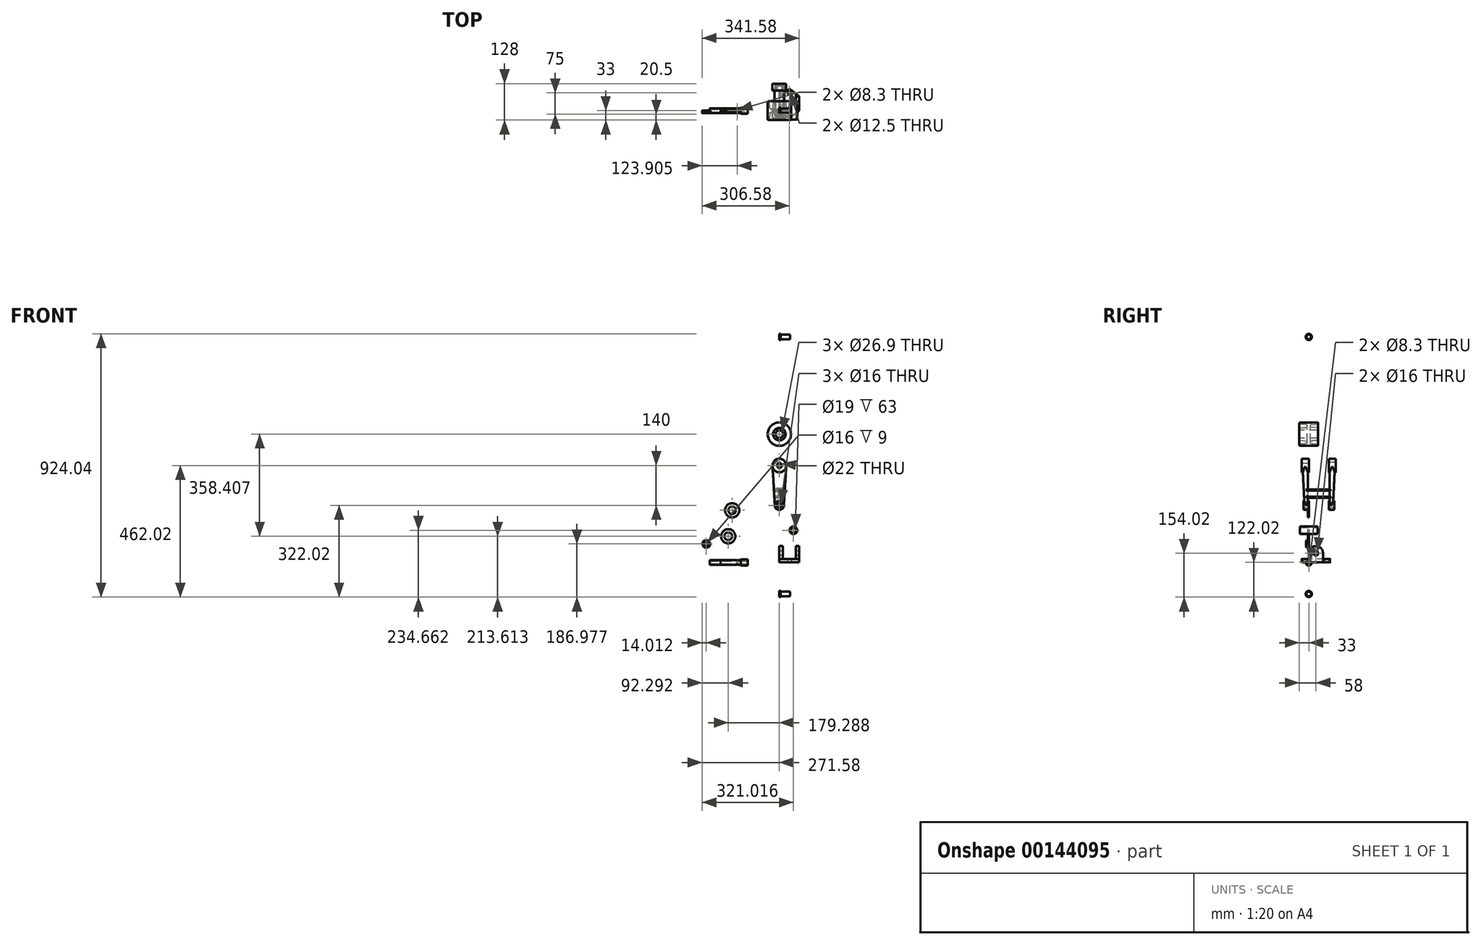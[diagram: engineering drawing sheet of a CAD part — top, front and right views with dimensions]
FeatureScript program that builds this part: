
annotation { "Feature Type Name" : "Feature", "Feature Type Description" : "" }
export const myFeature = defineFeature(function(context is Context, id is Id, definition is map)
    precondition{}
    {
        {
            var Q0;
            Q0=qCreatedBy(makeId("Top.planeOp"),FACE);
            var sketch = newSketch(context, id + "F0", { "sketchPlane" : qUnion([Q0])});
            skLineSegment(sketch, "E0", {"start": v(0, 0) * mm, "end": v(0, 50) * mm});
            skLineSegment(sketch, "E1", {"start": v(0, 50) * mm, "end": v(27.53, 71.9) * mm});
            skLineSegment(sketch, "E2", {"start": v(42.47, 71.9) * mm, "end": v(70, 50) * mm});
            skLineSegment(sketch, "E3", {"start": v(70, 50) * mm, "end": v(70, 0) * mm});
            skLineSegment(sketch, "E4", {"start": v(70, 0) * mm, "end": v(42.47, -21.9) * mm});
            skLineSegment(sketch, "E5", {"start": v(27.53, -21.9) * mm, "end": v(0, 0) * mm});
            skPoint(sketch, "E6.visualSharp", {"position": v(35, 77.83) * mm});
            skArc(sketch, "E6.filletArc", {"start": v(42.47, 71.9) * mm, "mid": v(35, 74.5) * mm, "end": v(27.53, 71.9) * mm});
            skPoint(sketch, "E7.visualSharp", {"position": v(35, -27.83) * mm});
            skArc(sketch, "E7.filletArc", {"start": v(27.53, -21.9) * mm, "mid": v(35, -24.5) * mm, "end": v(42.47, -21.9) * mm});
            skCircle(sketch, "E8", {"center": v(35, -12.5) * mm, "radius": 6.25 * mm});
            skCircle(sketch, "E9", {"center": v(35, 62.5) * mm, "radius": 6.25 * mm});
            skSolve(sketch);
        }
        {
            var Q0;
            Q0 = qSketchRegion(id + "F0", true);
            extrude(context, id + "F1", {"entities" : qUnion([Q0]), "depth" : 12 * mm});
        }
        {
            var Q0;
            Q0=qCreatedBy(makeId("Right.planeOp"),FACE);
            var sketch = newSketch(context, id + "F2", { "sketchPlane" : qUnion([Q0])});
            skLineSegment(sketch, "E10", {"start": v(0, 0) * mm, "end": v(0, 32) * mm});
            skLineSegment(sketch, "E11", {"start": v(50, 32) * mm, "end": v(50, 0) * mm});
            skArc(sketch, "E12", {"start": v(50, 32) * mm, "mid": v(25, 57) * mm, "end": v(0, 32) * mm});
            skCircle(sketch, "E13", {"center": v(25, 32) * mm, "radius": 8 * mm});
            skLineSegment(sketch, "E14", {"start": v(0, 0) * mm, "end": v(50, 0) * mm});
            skSolve(sketch);
        }
        {
            var Q0;
            Q0 = qSketchRegion(id + "F2", true);
            extrude(context, id + "F3", {"entities" : qUnion([Q0]), "operationType" : NewBodyOperationType.ADD, "depth" : 70 * mm});
        }
        {
            var Q0;
            Q0=qCreatedBy(makeId("Front.planeOp"),FACE);
            var sketch = newSketch(context, id + "F4", { "sketchPlane" : qUnion([Q0])});
            skLineSegment(sketch, "E15", {"start": v(0, 11.9) * mm, "end": v(70, 11.9) * mm, "construction": true});
            skLineSegment(sketch, "E16", {"start": v(12, 11.9) * mm, "end": v(12, 57.9) * mm});
            skLineSegment(sketch, "E17", {"start": v(12, 57.9) * mm, "end": v(58, 57.9) * mm});
            skLineSegment(sketch, "E18", {"start": v(58, 57.9) * mm, "end": v(58, 11.9) * mm});
            skLineSegment(sketch, "E19", {"start": v(12, 11.9) * mm, "end": v(58, 11.9) * mm});
            skSolve(sketch);
        }
        {
            var Q0;
            Q0 = qSketchRegion(id + "F4", true);
            extrude(context, id + "F5", {"entities" : qUnion([Q0]), "operationType" : NewBodyOperationType.REMOVE, "endBound" : BoundingType.THROUGH_ALL, "oppositeDirection" : true, "depth" : 25 * mm});
        }
        {
            var Q0;
            Q0=qCreatedBy(makeId("Front.planeOp"),FACE);
            var sketch = newSketch(context, id + "F6", { "sketchPlane" : qUnion([Q0])});
            skCircle(sketch, "E20", {"center": v(0, 200) * mm, "radius": 8 * mm});
            skCircle(sketch, "E21", {"center": v(0, 200) * mm, "radius": 16 * mm});
            skCircle(sketch, "E22", {"center": v(0, 340) * mm, "radius": 11 * mm});
            skCircle(sketch, "E23", {"center": v(0, 340) * mm, "radius": 24 * mm});
            skLineSegment(sketch, "E24", {"start": v(0, 200) * mm, "end": v(0, 200) * mm});
            skLineSegment(sketch, "E25", {"start": v(0, 200) * mm, "end": v(-54.61, 200) * mm, "construction": true});
            skLineSegment(sketch, "E26", {"start": v(0, 340) * mm, "end": v(0, 200) * mm, "construction": true});
            skSolve(sketch);
        }
        {
            var Q0;
            Q0=qCreatedBy(makeId("Right.planeOp"),FACE);
            var sketch = newSketch(context, id + "F7", { "sketchPlane" : qUnion([Q0])});
            skLineSegment(sketch, "E27", {"start": v(0, 0) * mm, "end": v(0, 463.45) * mm, "construction": true});
            skLineSegment(sketch, "E28", {"start": v(0, 463.45) * mm, "end": v(-31.5, 463.45) * mm});
            skLineSegment(sketch, "E29", {"start": v(0, 463.45) * mm, "end": v(31.5, 463.45) * mm});
            skLineSegment(sketch, "E30", {"start": v(-31.5, 463.45) * mm, "end": v(-31.5, 472) * mm});
            skLineSegment(sketch, "E31", {"start": v(31.5, 463.45) * mm, "end": v(31.5, 472) * mm});
            skLineSegment(sketch, "E32", {"start": v(0, 463.45) * mm, "end": v(0, 474) * mm, "construction": true});
            skLineSegment(sketch, "E33", {"start": v(0, 474) * mm, "end": v(-6, 474) * mm, "construction": true});
            skLineSegment(sketch, "E34", {"start": v(0, 474) * mm, "end": v(6, 474) * mm, "construction": true});
            skLineSegment(sketch, "E35", {"start": v(-31.5, 472) * mm, "end": v(-6, 474) * mm});
            skLineSegment(sketch, "E36", {"start": v(6, 474) * mm, "end": v(31.5, 472) * mm});
            skLineSegment(sketch, "E37", {"start": v(0, 450) * mm, "end": v(-20, 450) * mm});
            skLineSegment(sketch, "E38", {"start": v(0, 450) * mm, "end": v(20, 450) * mm});
            skLineSegment(sketch, "E39", {"start": v(6, 474) * mm, "end": v(6, 483) * mm});
            skLineSegment(sketch, "E40", {"start": v(-6, 474) * mm, "end": v(-6, 483) * mm});
            skLineSegment(sketch, "E41", {"start": v(-6, 483) * mm, "end": v(-33, 485) * mm});
            skLineSegment(sketch, "E42", {"start": v(-33, 485) * mm, "end": v(-33, 491) * mm});
            skLineSegment(sketch, "E43", {"start": v(-33, 491) * mm, "end": v(33, 491) * mm});
            skLineSegment(sketch, "E44", {"start": v(33, 491) * mm, "end": v(33, 485) * mm});
            skLineSegment(sketch, "E45", {"start": v(33, 485) * mm, "end": v(6, 483) * mm});
            skSolve(sketch);
        }
        {
            var Q0;
            Q0 = qSketchRegion(id + "F7", true);
            var Q1;
            Q1=sQuery(id+"F7.wireOp",EDGE,"E38");
            revolve(context, id + "F8", {"entities" : qUnion([Q0]), "axis" : qUnion([Q1]), "revolveType" : RevolveType.FULL});
        }
        {
            var Q0;
            Q0=makeQuery(id+"F8.opRevolve","SWEPT_EDGE",EDGE,{"disambiguationData":[OSD([sQuery(id+"F7.wireOp",EDGE,"E39"),sQuery(id+"F7.wireOp",EDGE,"E45")])]});
            var Q1;
            Q1=makeQuery(id+"F8.opRevolve","SWEPT_EDGE",EDGE,{"disambiguationData":[OSD([sQuery(id+"F7.wireOp",EDGE,"E36"),sQuery(id+"F7.wireOp",EDGE,"E39")])]});
            var Q2;
            Q2=makeQuery(id+"F8.opRevolve","SWEPT_EDGE",EDGE,{"disambiguationData":[OSD([sQuery(id+"F7.wireOp",EDGE,"E40"),sQuery(id+"F7.wireOp",EDGE,"E41")])]});
            var Q3;
            Q3=makeQuery(id+"F8.opRevolve","SWEPT_EDGE",EDGE,{"disambiguationData":[OSD([sQuery(id+"F7.wireOp",EDGE,"E35"),sQuery(id+"F7.wireOp",EDGE,"E40")])]});
            var Q4;
            Q4=makeQuery(id+"F8.opRevolve","SWEPT_FACE",FACE,{"disambiguationData":[OSD([sQuery(id+"F7.wireOp",EDGE,"E42")])]});
            var Q5;
            Q5=makeQuery(id+"F8.opRevolve","SWEPT_FACE",FACE,{"disambiguationData":[OSD([sQuery(id+"F7.wireOp",EDGE,"E44")])]});
            fillet(context, id + "F9", {"entities" : qUnion([Q0, Q1, Q2, Q3, Q4, Q5]), "radius" : 3 * mm, "tangentPropagation" : true, "allowEdgeOverflow" : false});
        }
        {
            var Q0;
            Q0=qCreatedBy(makeId("Front.planeOp"),FACE);
            var sketch = newSketch(context, id + "F10", { "sketchPlane" : qUnion([Q0])});
            skLineSegment(sketch, "E46", {"start": v(-110.67, 0) * mm, "end": v(-203.02, 0) * mm, "construction": true});
            skLineSegment(sketch, "E47.bottom", {"start": v(-110.67, 4.15) * mm, "end": v(-135.67, 4.15) * mm});
            skLineSegment(sketch, "E47.top", {"start": v(-110.67, 11) * mm, "end": v(-135.67, 11) * mm});
            skLineSegment(sketch, "E47.left", {"start": v(-110.67, 4.15) * mm, "end": v(-110.67, 11) * mm});
            skLineSegment(sketch, "E47.right", {"start": v(-135.67, 4.15) * mm, "end": v(-135.67, 11) * mm});
            skLineSegment(sketch, "E48.bottom", {"start": v(-135.67, 4.15) * mm, "end": v(-205.67, 4.15) * mm});
            skLineSegment(sketch, "E48.top", {"start": v(-135.67, 8.5) * mm, "end": v(-205.67, 8.5) * mm});
            skLineSegment(sketch, "E48.left", {"start": v(-135.67, 4.15) * mm, "end": v(-135.67, 8.5) * mm});
            skLineSegment(sketch, "E48.right", {"start": v(-205.67, 4.15) * mm, "end": v(-205.67, 8.5) * mm});
            skLineSegment(sketch, "E49.bottom", {"start": v(-205.67, 4.15) * mm, "end": v(-244.67, 4.15) * mm});
            skLineSegment(sketch, "E49.top", {"start": v(-205.67, 8) * mm, "end": v(-244.67, 8) * mm});
            skLineSegment(sketch, "E49.left", {"start": v(-205.67, 4.15) * mm, "end": v(-205.67, 8) * mm});
            skLineSegment(sketch, "E49.right", {"start": v(-244.67, 4.15) * mm, "end": v(-244.67, 8) * mm});
            skSolve(sketch);
        }
        {
            var Q0;
            Q0 = qSketchRegion(id + "F10", true);
            var Q1;
            Q1=sQuery(id+"F10.wireOp",EDGE,"E46");
            revolve(context, id + "F11", {"entities" : qUnion([Q0]), "axis" : qUnion([Q1]), "revolveType" : RevolveType.FULL});
        }
        {
            var Q0;
            Q0=qCreatedBy(makeId("Top.planeOp"),FACE);
            var sketch = newSketch(context, id + "F12", { "sketchPlane" : qUnion([Q0])});
            skLineSegment(sketch, "E50", {"start": v(-135.67, 0) * mm, "end": v(-147.67, 0) * mm});
            skCircle(sketch, "E51", {"center": v(-147.67, 0) * mm, "radius": 4.15 * mm});
            skSolve(sketch);
        }
        {
            var Q0;
            Q0=sQuery(id+"F6.wireOp",VERTEX,"E23.center");
            var Q1;
            Q1=qCreatedBy(makeId("Top.planeOp"),FACE);
            cPlane(context, id + "F13", {"entities" : qUnion([Q0, Q1]), "cplaneType" : CPlaneType.PLANE_POINT, "offset" : 25 * mm, "width" : 150 * mm, "height" : 150 * mm});
        }
        {
            var Q0;
            Q0=qCreatedBy(makeId("Front.planeOp"),FACE);
            var sketch = newSketch(context, id + "F14", { "sketchPlane" : qUnion([Q0])});
            skLineSegment(sketch, "E52", {"start": v(0, 0) * mm, "end": v(0, 112.64) * mm, "construction": true});
            skLineSegment(sketch, "E53", {"start": v(0, 112.64) * mm, "end": v(49.44, 112.64) * mm, "construction": true});
            skCircle(sketch, "E54", {"center": v(49.44, 112.64) * mm, "radius": 9.5 * mm});
            skCircle(sketch, "E55", {"center": v(49.44, 112.64) * mm, "radius": 13.45 * mm});
            skSolve(sketch);
        }
        {
            var Q0;
            Q0=makeQuery(id+"F6.imprint","IMPRINT",FACE,{"disambiguationData":[TD([[makeQuery(id+"F6.imprint","IMPRINT",EDGE,{"derivedFrom":sQuery(id+"F6.wireOp",EDGE,"E22")}),1.0]])]});
            var Q1;
            Q1=makeQuery(id+"F6.imprint","IMPRINT",FACE,{"disambiguationData":[TD([[makeQuery(id+"F6.imprint","IMPRINT",EDGE,{"derivedFrom":sQuery(id+"F6.wireOp",EDGE,"E22")}),-1.0]])]});
            extrude(context, id + "F15", {"entities" : qUnion([Q0, Q1]), "depth" : 25 * mm});
        }
        {
            var Q0;
            Q0=makeQuery(id+"F6.imprint","IMPRINT",FACE,{"disambiguationData":[TD([[makeQuery(id+"F6.imprint","IMPRINT",EDGE,{"derivedFrom":sQuery(id+"F6.wireOp",EDGE,"E20")}),1.0]])]});
            var Q1;
            Q1=makeQuery(id+"F6.imprint","IMPRINT",FACE,{"disambiguationData":[TD([[makeQuery(id+"F6.imprint","IMPRINT",EDGE,{"derivedFrom":sQuery(id+"F6.wireOp",EDGE,"E20")}),-1.0]])]});
            extrude(context, id + "F16", {"entities" : qUnion([Q0, Q1]), "depth" : 19 * mm});
        }
        {
            var Q0;
            Q0 = qSketchRegion(id + "F14", true);
            extrude(context, id + "F17", {"entities" : qUnion([Q0]), "endBound" : BoundingType.SYMMETRIC, "depth" : 63 * mm});
        }
        {
            var Q0;
            Q0=qCreatedBy(id+"F13.planeOp",FACE);
            var sketch = newSketch(context, id + "F18", { "sketchPlane" : qUnion([Q0])});
            skEllipse(sketch, "E56", {"center": v(0, -12.5) * mm, "majorRadius": 24 * mm, "minorRadius": 9.5 * mm, "majorAxis": v(1, 0)});
            skPoint(sketch, "E57", {"position": v(0, -3) * mm});
            skLineSegment(sketch, "E58", {"start": v(24, 0) * mm, "end": v(24, -25) * mm, "construction": true});
            skSolve(sketch);
        }
        {
            var Q0;
            Q0 = qSketchRegion(id + "F12", true);
            extrude(context, id + "F19", {"entities" : qUnion([Q0]), "operationType" : NewBodyOperationType.REMOVE, "depth" : 25 * mm, "hasSecondDirection" : true, "secondDirectionOppositeDirection" : true, "secondDirectionDepth" : 25 * mm});
        }
        {
            var Q0;
            Q0=sQuery(id+"F6.wireOp",VERTEX,"E21.center");
            var Q1;
            Q1=qCreatedBy(makeId("Top.planeOp"),FACE);
            cPlane(context, id + "F20", {"entities" : qUnion([Q0, Q1]), "cplaneType" : CPlaneType.PLANE_POINT, "offset" : 25 * mm, "width" : 150 * mm, "height" : 150 * mm});
        }
        {
            var Q0;
            Q0=qCreatedBy(id+"F20.planeOp",FACE);
            var sketch = newSketch(context, id + "F21", { "sketchPlane" : qUnion([Q0])});
            skEllipse(sketch, "E59", {"center": v(0, -9) * mm, "majorRadius": 16 * mm, "minorRadius": 6 * mm, "majorAxis": v(1, 0)});
            skPoint(sketch, "E60", {"position": v(0, -3) * mm});
            skLineSegment(sketch, "E61", {"start": v(16, 0) * mm, "end": v(16, -19) * mm, "construction": true});
            skSolve(sketch);
        }
        {
            var Q0;
            Q0=makeQuery(id+"F18.imprint","IMPRINT",FACE,{"disambiguationData":[TD([[makeQuery(id+"F18.imprint","IMPRINT",EDGE,{"derivedFrom":sQuery(id+"F18.wireOp",EDGE,"E56")}),1.0]])]});
            var Q1;
            Q1=makeQuery(id+"F21.imprint","IMPRINT",FACE,{"disambiguationData":[TD([[makeQuery(id+"F21.imprint","IMPRINT",EDGE,{"derivedFrom":sQuery(id+"F21.wireOp",EDGE,"E59")}),1.0]])]});
            loft(context, id + "F22", {"operationType" : NewBodyOperationType.ADD, "sheetProfilesArray" : [{ "sheetProfileEntities" : qUnion([Q0]) }, { "sheetProfileEntities" : qUnion([Q1]) }]});
        }
        {
            var Q0;
            Q0=makeQuery(id+"F6.imprint","IMPRINT",FACE,{"disambiguationData":[TD([[makeQuery(id+"F6.imprint","IMPRINT",EDGE,{"derivedFrom":sQuery(id+"F6.wireOp",EDGE,"E22")}),1.0]])]});
            var Q1;
            Q1=makeQuery(id+"F6.imprint","IMPRINT",FACE,{"disambiguationData":[TD([[makeQuery(id+"F6.imprint","IMPRINT",EDGE,{"derivedFrom":sQuery(id+"F6.wireOp",EDGE,"E20")}),1.0]])]});
            extrude(context, id + "F23", {"entities" : qUnion([Q0, Q1]), "operationType" : NewBodyOperationType.REMOVE, "endBound" : BoundingType.THROUGH_ALL, "depth" : 25 * mm});
        }
        {
            var Q0;
            Q0=qCreatedBy(makeId("Front.planeOp"),FACE);
            var sketch = newSketch(context, id + "F24", { "sketchPlane" : qUnion([Q0])});
            skCircle(sketch, "E62", {"center": v(-179.29, 91.6) * mm, "radius": 25 * mm});
            skCircle(sketch, "E63", {"center": v(-179.29, 91.6) * mm, "radius": 13.45 * mm});
            skCircle(sketch, "E64", {"center": v(-165.64, 182.83) * mm, "radius": 25 * mm});
            skCircle(sketch, "E65", {"center": v(-165.64, 182.83) * mm, "radius": 13.45 * mm});
            skSolve(sketch);
        }
        {
            var Q0;
            Q0 = qSketchRegion(id + "F24", true);
            extrude(context, id + "F25", {"entities" : qUnion([Q0]), "depth" : 3 * mm});
        }
        {
            var Q0;
            Q0=qCreatedBy(makeId("Front.planeOp"),FACE);
            var sketch = newSketch(context, id + "F26", { "sketchPlane" : qUnion([Q0])});
            skLineSegment(sketch, "E66", {"start": v(-264.37, 77.03) * mm, "end": v(-249.51, 77.03) * mm});
            skLineSegment(sketch, "E67", {"start": v(-249.51, 77.03) * mm, "end": v(-242.3, 65.03) * mm});
            skLineSegment(sketch, "E68", {"start": v(-242.3, 65.03) * mm, "end": v(-249.51, 53.03) * mm});
            skLineSegment(sketch, "E69", {"start": v(-249.51, 53.03) * mm, "end": v(-264.37, 53.03) * mm});
            skLineSegment(sketch, "E70", {"start": v(-264.37, 53.03) * mm, "end": v(-271.58, 65.03) * mm});
            skLineSegment(sketch, "E71", {"start": v(-271.58, 65.03) * mm, "end": v(-264.37, 77.03) * mm});
            skCircle(sketch, "E72", {"center": v(-257.57, 64.96) * mm, "radius": 8 * mm});
            skSolve(sketch);
        }
        {
            var Q0;
            Q0 = qSketchRegion(id + "F26", true);
            extrude(context, id + "F27", {"entities" : qUnion([Q0]), "depth" : 9 * mm});
        }
        {
            var Q0;
            Q0=makeQuery(id+"F27.opExtrude","CAP_EDGE",EDGE,{"disambiguationData":[OSD([sQuery(id+"F26.wireOp",EDGE,"E66")])],"isStart":false});
            var Q1;
            Q1=makeQuery(id+"F27.opExtrude","CAP_EDGE",EDGE,{"disambiguationData":[OSD([sQuery(id+"F26.wireOp",EDGE,"E71")])],"isStart":false});
            var Q2;
            Q2=makeQuery(id+"F27.opExtrude","CAP_EDGE",EDGE,{"disambiguationData":[OSD([sQuery(id+"F26.wireOp",EDGE,"E70")])],"isStart":false});
            var Q3;
            Q3=makeQuery(id+"F27.opExtrude","CAP_EDGE",EDGE,{"disambiguationData":[OSD([sQuery(id+"F26.wireOp",EDGE,"E69")])],"isStart":false});
            var Q4;
            Q4=makeQuery(id+"F27.opExtrude","CAP_EDGE",EDGE,{"disambiguationData":[OSD([sQuery(id+"F26.wireOp",EDGE,"E68")])],"isStart":false});
            var Q5;
            Q5=makeQuery(id+"F27.opExtrude","CAP_EDGE",EDGE,{"disambiguationData":[OSD([sQuery(id+"F26.wireOp",EDGE,"E67")])],"isStart":false});
            var Q6;
            Q6=makeQuery(id+"F27.opExtrude","CAP_EDGE",EDGE,{"disambiguationData":[OSD([sQuery(id+"F26.wireOp",EDGE,"E67")])],"isStart":true});
            var Q7;
            Q7=makeQuery(id+"F27.opExtrude","CAP_EDGE",EDGE,{"disambiguationData":[OSD([sQuery(id+"F26.wireOp",EDGE,"E70")])],"isStart":true});
            var Q8;
            Q8=makeQuery(id+"F27.opExtrude","CAP_EDGE",EDGE,{"disambiguationData":[OSD([sQuery(id+"F26.wireOp",EDGE,"E71")])],"isStart":true});
            var Q9;
            Q9=makeQuery(id+"F27.opExtrude","CAP_EDGE",EDGE,{"disambiguationData":[OSD([sQuery(id+"F26.wireOp",EDGE,"E66")])],"isStart":true});
            var Q10;
            Q10=makeQuery(id+"F27.opExtrude","CAP_EDGE",EDGE,{"disambiguationData":[OSD([sQuery(id+"F26.wireOp",EDGE,"E69")])],"isStart":true});
            var Q11;
            Q11=makeQuery(id+"F27.opExtrude","CAP_EDGE",EDGE,{"disambiguationData":[OSD([sQuery(id+"F26.wireOp",EDGE,"E68")])],"isStart":true});
            fillet(context, id + "F28", {"entities" : qUnion([Q0, Q1, Q2, Q3, Q4, Q5, Q6, Q7, Q8, Q9, Q10, Q11]), "radius" : 1.5 * mm, "tangentPropagation" : true, "allowEdgeOverflow" : false});
        }
        {
            var Q0;
            Q0=sQuery(id+"F21.wireOp",VERTEX,"E59.center");
            var Q1;
            Q1=qCreatedBy(makeId("Front.planeOp"),FACE);
            cPlane(context, id + "F29", {"entities" : qUnion([Q0, Q1]), "cplaneType" : CPlaneType.PLANE_POINT, "offset" : 25 * mm, "width" : 150 * mm, "height" : 150 * mm});
        }
        {
            var Q0;
            Q0=qCreatedBy(makeId("Right.planeOp"),FACE);
            var sketch = newSketch(context, id + "F30", { "sketchPlane" : qUnion([Q0])});
            skPoint(sketch, "E73.0", {"position": v(0, 200) * mm});
            skPoint(sketch, "E74", {"position": v(35, 200) * mm});
            skSolve(sketch);
        }
        {
            var Q0;
            Q0=sQuery(id+"F30.wireOp",VERTEX,"E74");
            var Q1;
            Q1=qCreatedBy(makeId("Front.planeOp"),FACE);
            cPlane(context, id + "F31", {"entities" : qUnion([Q0, Q1]), "cplaneType" : CPlaneType.PLANE_POINT, "offset" : 25 * mm, "width" : 150 * mm, "height" : 150 * mm});
        }
        {
            var Q0;
            Q0=makeQuery(id+"F15.opExtrude","SWEPT_BODY",BODY,{"disambiguationData":[OSD([sQuery(id+"F6.wireOp",EDGE,"E23")])]});
            var Q1;
            Q1=qCreatedBy(id+"F31.planeOp",FACE);
            mirror(context, id + "F32", {"entities" : qUnion([Q0]), "mirrorPlane" : qUnion([Q1])});
        }
        {
            var Q0;
            Q0=qCreatedBy(id+"F29.planeOp",FACE);
            var sketch = newSketch(context, id + "F33", { "sketchPlane" : qUnion([Q0])});
            skPoint(sketch, "E75.0", {"position": v(0, 200) * mm});
            skLineSegment(sketch, "E76", {"start": v(0, 200) * mm, "end": v(0, 226) * mm, "construction": true});
            skLineSegment(sketch, "E77", {"start": v(0, 226) * mm, "end": v(-17, 226) * mm});
            skLineSegment(sketch, "E78", {"start": v(-17, 226) * mm, "end": v(-17, 230) * mm});
            skLineSegment(sketch, "E79", {"start": v(-17, 230) * mm, "end": v(-2, 230) * mm});
            skLineSegment(sketch, "E80", {"start": v(-2, 230) * mm, "end": v(-2, 252) * mm});
            skLineSegment(sketch, "E81", {"start": v(-2, 252) * mm, "end": v(-17, 252) * mm});
            skLineSegment(sketch, "E82", {"start": v(-17, 252) * mm, "end": v(-17, 256) * mm});
            skLineSegment(sketch, "E83", {"start": v(-17, 256) * mm, "end": v(17, 256) * mm});
            skLineSegment(sketch, "E84", {"start": v(17, 256) * mm, "end": v(17, 252) * mm});
            skLineSegment(sketch, "E85", {"start": v(17, 252) * mm, "end": v(2, 252) * mm});
            skLineSegment(sketch, "E86", {"start": v(2, 252) * mm, "end": v(2, 230) * mm});
            skLineSegment(sketch, "E87", {"start": v(2, 230) * mm, "end": v(17, 230) * mm});
            skLineSegment(sketch, "E88", {"start": v(17, 230) * mm, "end": v(17, 226) * mm});
            skLineSegment(sketch, "E89", {"start": v(0, 226) * mm, "end": v(17, 226) * mm});
            skSolve(sketch);
        }
        {
            var Q0;
            Q0 = qSketchRegion(id + "F33", true);
            var Q1;
            Q1=makeQuery(id+"F32.opPattern","COPY",BODY,{"derivedFrom":makeQuery(id+"F15.opExtrude","SWEPT_BODY",BODY,{"disambiguationData":[OSD([sQuery(id+"F6.wireOp",EDGE,"E23")])]}),"instanceName":"1"});
            extrude(context, id + "F34", {"entities" : qUnion([Q0]), "operationType" : NewBodyOperationType.ADD, "endBound" : BoundingType.UP_TO_BODY, "oppositeDirection" : true, "endBoundEntityBody" : qUnion([Q1]), "depth" : 25 * mm});
        }
        {
            var Q0;
            Q0=makeQuery(id+"F34.opExtrude","TWEAK_EDGE",EDGE,{"derivedFrom":[makeQuery(id+"F32.opPattern","COPY",FACE,{"derivedFrom":makeQuery(id+"F22.opLoft","SWEPT_FACE",FACE,{"disambiguationData":[OSD([sQuery(id+"F18.wireOp",EDGE,"E56"),sQuery(id+"F21.wireOp",EDGE,"E59")])]}),"instanceName":"1"}),makeQuery(id+"F33.imprint","IMPRINT",EDGE,{"derivedFrom":sQuery(id+"F33.wireOp",EDGE,"E81")})]});
            var Q1;
            Q1=makeQuery(id+"F34.opExtrude","TWEAK_EDGE",EDGE,{"derivedFrom":[makeQuery(id+"F32.opPattern","COPY",FACE,{"derivedFrom":makeQuery(id+"F22.opLoft","SWEPT_FACE",FACE,{"disambiguationData":[OSD([sQuery(id+"F18.wireOp",EDGE,"E56"),sQuery(id+"F21.wireOp",EDGE,"E59")])]}),"instanceName":"1"}),makeQuery(id+"F33.imprint","IMPRINT",EDGE,{"derivedFrom":sQuery(id+"F33.wireOp",EDGE,"E80")})]});
            var Q2;
            Q2=makeQuery(id+"F34.opExtrude","TWEAK_EDGE",EDGE,{"derivedFrom":[makeQuery(id+"F32.opPattern","COPY",FACE,{"derivedFrom":makeQuery(id+"F22.opLoft","SWEPT_FACE",FACE,{"disambiguationData":[OSD([sQuery(id+"F18.wireOp",EDGE,"E56"),sQuery(id+"F21.wireOp",EDGE,"E59")])]}),"instanceName":"1"}),makeQuery(id+"F33.imprint","IMPRINT",EDGE,{"derivedFrom":sQuery(id+"F33.wireOp",EDGE,"E79")})]});
            var Q3;
            Q3=makeQuery(id+"F34.opExtrude","SWEPT_EDGE",EDGE,{"disambiguationData":[OSD([sQuery(id+"F33.wireOp",EDGE,"E79"),sQuery(id+"F33.wireOp",EDGE,"E80")])]});
            var Q4;
            Q4=makeQuery(id+"F34.boolean.opBoolean","INTERSECT",EDGE,{"derivedFrom":[makeQuery(id+"F22.opLoft","SWEPT_FACE",FACE,{"disambiguationData":[OSD([sQuery(id+"F18.wireOp",EDGE,"E56"),sQuery(id+"F21.wireOp",EDGE,"E59")])]}),makeQuery(id+"F34.opExtrude","SWEPT_FACE",FACE,{"disambiguationData":[OSD([sQuery(id+"F33.wireOp",EDGE,"E79")])]})]});
            var Q5;
            Q5=makeQuery(id+"F34.boolean.opBoolean","INTERSECT",EDGE,{"derivedFrom":[makeQuery(id+"F22.opLoft","SWEPT_FACE",FACE,{"disambiguationData":[OSD([sQuery(id+"F18.wireOp",EDGE,"E56"),sQuery(id+"F21.wireOp",EDGE,"E59")])]}),makeQuery(id+"F34.opExtrude","SWEPT_FACE",FACE,{"disambiguationData":[OSD([sQuery(id+"F33.wireOp",EDGE,"E80")])]})]});
            var Q6;
            Q6=makeQuery(id+"F34.boolean.opBoolean","INTERSECT",EDGE,{"derivedFrom":[makeQuery(id+"F22.opLoft","SWEPT_FACE",FACE,{"disambiguationData":[OSD([sQuery(id+"F18.wireOp",EDGE,"E56"),sQuery(id+"F21.wireOp",EDGE,"E59")])]}),makeQuery(id+"F34.opExtrude","SWEPT_FACE",FACE,{"disambiguationData":[OSD([sQuery(id+"F33.wireOp",EDGE,"E83")])]})]});
            var Q7;
            Q7=makeQuery(id+"F34.boolean.opBoolean","INTERSECT",EDGE,{"derivedFrom":[makeQuery(id+"F22.opLoft","SWEPT_FACE",FACE,{"disambiguationData":[OSD([sQuery(id+"F18.wireOp",EDGE,"E56"),sQuery(id+"F21.wireOp",EDGE,"E59")])]}),makeQuery(id+"F34.opExtrude","SWEPT_FACE",FACE,{"disambiguationData":[OSD([sQuery(id+"F33.wireOp",EDGE,"E81")])]})]});
            var Q8;
            Q8=makeQuery(id+"F34.opExtrude","TWEAK_EDGE",EDGE,{"derivedFrom":[makeQuery(id+"F32.opPattern","COPY",FACE,{"derivedFrom":makeQuery(id+"F22.opLoft","SWEPT_FACE",FACE,{"disambiguationData":[OSD([sQuery(id+"F18.wireOp",EDGE,"E56"),sQuery(id+"F21.wireOp",EDGE,"E59")])]}),"instanceName":"1"}),makeQuery(id+"F33.imprint","IMPRINT",EDGE,{"derivedFrom":sQuery(id+"F33.wireOp",EDGE,"E83")})]});
            var Q9;
            Q9=makeQuery(id+"F34.opExtrude","TWEAK_EDGE",EDGE,{"derivedFrom":[makeQuery(id+"F32.opPattern","COPY",FACE,{"derivedFrom":makeQuery(id+"F22.opLoft","SWEPT_FACE",FACE,{"disambiguationData":[OSD([sQuery(id+"F18.wireOp",EDGE,"E56"),sQuery(id+"F21.wireOp",EDGE,"E59")])]}),"instanceName":"1"}),makeQuery(id+"F33.imprint","IMPRINT",EDGE,{"derivedFrom":sQuery(id+"F33.wireOp",EDGE,"E87")})]});
            var Q10;
            Q10=makeQuery(id+"F34.opExtrude","TWEAK_EDGE",EDGE,{"derivedFrom":[makeQuery(id+"F32.opPattern","COPY",FACE,{"derivedFrom":makeQuery(id+"F22.opLoft","SWEPT_FACE",FACE,{"disambiguationData":[OSD([sQuery(id+"F18.wireOp",EDGE,"E56"),sQuery(id+"F21.wireOp",EDGE,"E59")])]}),"instanceName":"1"}),makeQuery(id+"F33.imprint","IMPRINT",EDGE,{"derivedFrom":sQuery(id+"F33.wireOp",EDGE,"E86")})]});
            var Q11;
            Q11=makeQuery(id+"F34.opExtrude","TWEAK_EDGE",EDGE,{"derivedFrom":[makeQuery(id+"F32.opPattern","COPY",FACE,{"derivedFrom":makeQuery(id+"F22.opLoft","SWEPT_FACE",FACE,{"disambiguationData":[OSD([sQuery(id+"F18.wireOp",EDGE,"E56"),sQuery(id+"F21.wireOp",EDGE,"E59")])]}),"instanceName":"1"}),makeQuery(id+"F33.imprint","IMPRINT",EDGE,{"derivedFrom":sQuery(id+"F33.wireOp",EDGE,"E85")})]});
            var Q12;
            Q12=makeQuery(id+"F34.opExtrude","SWEPT_EDGE",EDGE,{"disambiguationData":[OSD([sQuery(id+"F33.wireOp",EDGE,"E85"),sQuery(id+"F33.wireOp",EDGE,"E86")])]});
            var Q13;
            Q13=makeQuery(id+"F34.opExtrude","SWEPT_EDGE",EDGE,{"disambiguationData":[OSD([sQuery(id+"F33.wireOp",EDGE,"E86"),sQuery(id+"F33.wireOp",EDGE,"E87")])]});
            var Q14;
            Q14=makeQuery(id+"F34.boolean.opBoolean","INTERSECT",EDGE,{"derivedFrom":[makeQuery(id+"F22.opLoft","SWEPT_FACE",FACE,{"disambiguationData":[OSD([sQuery(id+"F18.wireOp",EDGE,"E56"),sQuery(id+"F21.wireOp",EDGE,"E59")])]}),makeQuery(id+"F34.opExtrude","SWEPT_FACE",FACE,{"disambiguationData":[OSD([sQuery(id+"F33.wireOp",EDGE,"E87")])]})]});
            var Q15;
            Q15=makeQuery(id+"F34.boolean.opBoolean","INTERSECT",EDGE,{"derivedFrom":[makeQuery(id+"F22.opLoft","SWEPT_FACE",FACE,{"disambiguationData":[OSD([sQuery(id+"F18.wireOp",EDGE,"E56"),sQuery(id+"F21.wireOp",EDGE,"E59")])]}),makeQuery(id+"F34.opExtrude","SWEPT_FACE",FACE,{"disambiguationData":[OSD([sQuery(id+"F33.wireOp",EDGE,"E86")])]})]});
            var Q16;
            Q16=makeQuery(id+"F34.boolean.opBoolean","INTERSECT",EDGE,{"derivedFrom":[makeQuery(id+"F22.opLoft","SWEPT_FACE",FACE,{"disambiguationData":[OSD([sQuery(id+"F18.wireOp",EDGE,"E56"),sQuery(id+"F21.wireOp",EDGE,"E59")])]}),makeQuery(id+"F34.opExtrude","SWEPT_FACE",FACE,{"disambiguationData":[OSD([sQuery(id+"F33.wireOp",EDGE,"E85")])]})]});
            fillet(context, id + "F35", {"entities" : qUnion([Q0, Q1, Q2, Q3, Q4, Q5, Q6, Q7, Q8, Q9, Q10, Q11, Q12, Q13, Q14, Q15, Q16]), "radius" : 3 * mm, "tangentPropagation" : true, "allowEdgeOverflow" : false});
        }
        {
            var Q0;
            Q0=qCreatedBy(makeId("Front.planeOp"),FACE);
            var sketch = newSketch(context, id + "F36", { "sketchPlane" : qUnion([Q0])});
            skPoint(sketch, "E90.0", {"position": v(0, 340) * mm});
            skCircle(sketch, "E91", {"center": v(0, 340) * mm, "radius": 8 * mm});
            skCircle(sketch, "E92", {"center": v(0, 340) * mm, "radius": 11 * mm});
            skSolve(sketch);
        }
        {
            var Q0;
            Q0 = qSketchRegion(id + "F36", true);
            var Q1;
            Q1=makeQuery(id+"F15.opExtrude","CAP_FACE",FACE,{"disambiguationData":[OSD([sQuery(id+"F6.wireOp",EDGE,"E23")])],"isStart":false});
            extrude(context, id + "F37", {"entities" : qUnion([Q0]), "operationType" : NewBodyOperationType.ADD, "endBound" : BoundingType.UP_TO_SURFACE, "endBoundEntityFace" : qUnion([Q1]), "depth" : 25 * mm});
        }
        {
            var Q0;
            Q0=qCreatedBy(makeId("Right.planeOp"),FACE);
            var sketch = newSketch(context, id + "F38", { "sketchPlane" : qUnion([Q0])});
            skCircle(sketch, "E93", {"center": v(0, -111.02) * mm, "radius": 11 * mm});
            skSolve(sketch);
        }
        {
            var Q0;
            Q0 = qSketchRegion(id + "F38", true);
            extrude(context, id + "F39", {"entities" : qUnion([Q0]), "depth" : 5 * mm});
        }
        {
            var Q0;
            Q0=makeQuery(id+"F39.opExtrude","CAP_FACE",FACE,{"disambiguationData":[OSD([sQuery(id+"F38.wireOp",EDGE,"E93")])],"isStart":false});
            var sketch = newSketch(context, id + "F40", { "sketchPlane" : qUnion([Q0])});
            skCircle(sketch, "E94", {"center": v(0, -111.02) * mm, "radius": 8 * mm});
            skSolve(sketch);
        }
        {
            var Q0;
            Q0 = qSketchRegion(id + "F40", true);
            extrude(context, id + "F41", {"entities" : qUnion([Q0]), "operationType" : NewBodyOperationType.ADD, "depth" : 33 * mm});
        }
        {
            var Q0;
            Q0=makeQuery(id+"F39.opExtrude","SWEPT_BODY",BODY,{"disambiguationData":[OSD([sQuery(id+"F38.wireOp",EDGE,"E93")])]});
            var Q1;
            Q1=qCreatedBy(id+"F13.planeOp",FACE);
            mirror(context, id + "F42", {"entities" : qUnion([Q0]), "mirrorPlane" : qUnion([Q1])});
        }
    });
